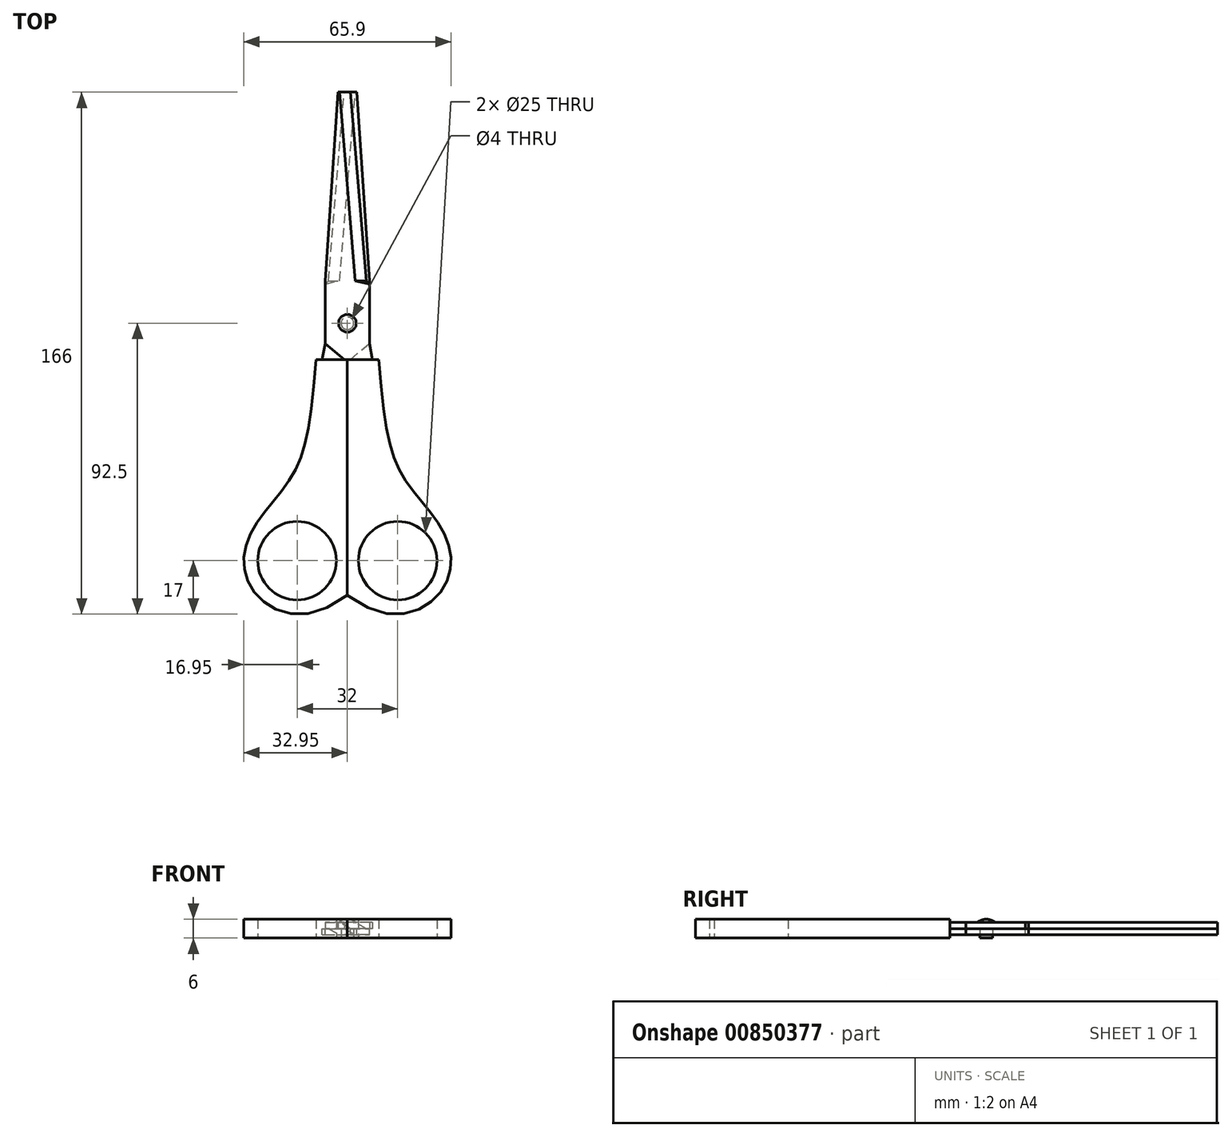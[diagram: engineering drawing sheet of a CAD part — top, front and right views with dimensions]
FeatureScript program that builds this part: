
annotation { "Feature Type Name" : "Feature", "Feature Type Description" : "" }
export const myFeature = defineFeature(function(context is Context, id is Id, definition is map)
    precondition{}
    {
        {
            var Q0;
            Q0=qCreatedBy(makeId("Top.planeOp"),FACE);
            var sketch = newSketch(context, id + "F0", { "sketchPlane" : qUnion([Q0])});
            skLineSegment(sketch, "E0", {"start": v(10, 0) * mm, "end": v(0, 0) * mm});
            skLineSegment(sketch, "E1", {"start": v(0, 0) * mm, "end": v(0, -75) * mm});
            skFitSpline(sketch, "E2", {"points": [v(10, 0) * mm, v(18.6, -38.65) * mm, v(31.21, -56.2) * mm, v(29.97, -73.56) * mm, v(0, -75) * mm], "startDerivative": vector(15.7, -213.23) * mm, "endDerivative": vector(-155.18, 117.57) * mm});
            skSolve(sketch);
        }
        {
            var Q0;
            Q0=qSketchRegion(id+"F0",true);
            extrude(context, id + "F1", {"entities" : qUnion([Q0]), "depth" : 6 * mm, "offsetDistance" : 25 * mm});
        }
        {
            var Q0;
            Q0=qCreatedBy(makeId("Top.planeOp"),FACE);
            var sketch = newSketch(context, id + "F2", { "sketchPlane" : qUnion([Q0])});
            skCircle(sketch, "E3", {"center": v(16, -64) * mm, "radius": 12.5 * mm});
            skSolve(sketch);
        }
        {
            var Q0;
            Q0=qSketchRegion(id+"F2",true);
            extrude(context, id + "F3", {"entities" : qUnion([Q0]), "depth" : 6 * mm, "offsetDistance" : 25 * mm});
        }
        {
            var Q0;
            Q0=makeQuery(id+"F3.opExtrude","SWEPT_BODY",BODY,{"disambiguationData":[OSD([sQuery(id+"F2.wireOp",EDGE,"E3")])]});
            var Q1;
            Q1=makeQuery(id+"F1.opExtrude","SWEPT_BODY",BODY,{"disambiguationData":[OSD([sQuery(id+"F0.wireOp",EDGE,"E0"),sQuery(id+"F0.wireOp",EDGE,"E1"),sQuery(id+"F0.wireOp",EDGE,"E2")])]});
            booleanBodies(context, id + "F4", {"operationType" : BooleanOperationType.SUBTRACTION, "tools" : qUnion([Q0]), "targets" : qUnion([Q1])});
        }
        {
            var Q0;
            Q0=makeQuery(id+"F1.opExtrude","SWEPT_BODY",BODY,{"disambiguationData":[OSD([sQuery(id+"F0.wireOp",EDGE,"E0"),sQuery(id+"F0.wireOp",EDGE,"E1"),sQuery(id+"F0.wireOp",EDGE,"E2")])]});
            var Q1;
            Q1=qCreatedBy(makeId("Right.planeOp"),FACE);
            mirror(context, id + "F5", {"entities" : qUnion([Q0]), "mirrorPlane" : qUnion([Q1])});
        }
        {
            var Q0;
            Q0=qCreatedBy(makeId("Top.planeOp"),FACE);
            cPlane(context, id + "F6", {"entities" : qUnion([Q0]), "cplaneType" : CPlaneType.OFFSET, "offset" : 3 * mm, "width" : 150 * mm, "height" : 150 * mm});
        }
        {
            var Q0;
            Q0=qCreatedBy(makeId("Front.planeOp"),FACE);
            cPlane(context, id + "F7", {"entities" : qUnion([Q0]), "cplaneType" : CPlaneType.OFFSET, "offset" : 5 * mm, "oppositeDirection" : true, "width" : 150 * mm, "height" : 150 * mm});
        }
        {
            var Q0;
            Q0=qCreatedBy(makeId("Front.planeOp"),FACE);
            cPlane(context, id + "F8", {"entities" : qUnion([Q0]), "cplaneType" : CPlaneType.OFFSET, "offset" : 15 * mm, "oppositeDirection" : true, "width" : 150 * mm, "height" : 150 * mm});
        }
        {
            var Q0;
            Q0=qCreatedBy(makeId("Front.planeOp"),FACE);
            cPlane(context, id + "F9", {"entities" : qUnion([Q0]), "cplaneType" : CPlaneType.OFFSET, "offset" : 25 * mm, "oppositeDirection" : true, "width" : 150 * mm, "height" : 150 * mm});
        }
        {
            var Q0;
            Q0=qCreatedBy(makeId("Front.planeOp"),FACE);
            cPlane(context, id + "F10", {"entities" : qUnion([Q0]), "cplaneType" : CPlaneType.OFFSET, "offset" : 85 * mm, "oppositeDirection" : true, "width" : 150 * mm, "height" : 150 * mm});
        }
        {
            var Q0;
            Q0=qCreatedBy(makeId("Front.planeOp"),FACE);
            cPlane(context, id + "F11", {"entities" : qUnion([Q0]), "cplaneType" : CPlaneType.OFFSET, "offset" : 24 * mm, "oppositeDirection" : true, "width" : 150 * mm, "height" : 150 * mm});
        }
        {
            var Q0;
            Q0=qCreatedBy(makeId("Front.planeOp"),FACE);
            var sketch = newSketch(context, id + "F12", { "sketchPlane" : qUnion([Q0])});
            skLineSegment(sketch, "E4.bottom", {"start": v(8, 5) * mm, "end": v(-1, 5) * mm});
            skLineSegment(sketch, "E4.top", {"start": v(8, 3) * mm, "end": v(-1, 3) * mm});
            skLineSegment(sketch, "E4.left", {"start": v(8, 5) * mm, "end": v(8, 3) * mm});
            skLineSegment(sketch, "E4.right", {"start": v(-1, 5) * mm, "end": v(-1, 3) * mm});
            skSolve(sketch);
        }
        {
            var Q0;
            Q0=qCreatedBy(id+"F7.planeOp",FACE);
            var sketch = newSketch(context, id + "F13", { "sketchPlane" : qUnion([Q0])});
            skLineSegment(sketch, "E5.bottom", {"start": v(7, 5) * mm, "end": v(-7, 5) * mm});
            skLineSegment(sketch, "E5.top", {"start": v(7, 3) * mm, "end": v(-7, 3) * mm});
            skLineSegment(sketch, "E5.left", {"start": v(7, 5) * mm, "end": v(7, 3) * mm});
            skLineSegment(sketch, "E5.right", {"start": v(-7, 5) * mm, "end": v(-7, 3) * mm});
            skSolve(sketch);
        }
        {
            var Q0;
            Q0=qCreatedBy(id+"F10.planeOp",FACE);
            var sketch = newSketch(context, id + "F14", { "sketchPlane" : qUnion([Q0])});
            skLineSegment(sketch, "E6", {"start": v(-2.5, 5) * mm, "end": v(-3, 5) * mm});
            skLineSegment(sketch, "E7", {"start": v(-3, 5) * mm, "end": v(-3, 3) * mm});
            skLineSegment(sketch, "E8", {"start": v(-3, 3) * mm, "end": v(1, 3) * mm});
            skLineSegment(sketch, "E9", {"start": v(1, 3) * mm, "end": v(-2.5, 5) * mm});
            skSolve(sketch);
        }
        {
            var Q0;
            Q0=qCreatedBy(id+"F8.planeOp",FACE);
            var sketch = newSketch(context, id + "F15", { "sketchPlane" : qUnion([Q0])});
            skLineSegment(sketch, "E10", {"start": v(-7, 5) * mm, "end": v(6, 5) * mm});
            skLineSegment(sketch, "E11", {"start": v(6, 5) * mm, "end": v(6, 3) * mm});
            skLineSegment(sketch, "E12", {"start": v(6, 3) * mm, "end": v(-7, 3) * mm});
            skLineSegment(sketch, "E13", {"start": v(-7, 3) * mm, "end": v(-7, 5) * mm});
            skSolve(sketch);
        }
        {
            var Q0;
            Q0=qCreatedBy(id+"F9.planeOp",FACE);
            var sketch = newSketch(context, id + "F16", { "sketchPlane" : qUnion([Q0])});
            skLineSegment(sketch, "E14", {"start": v(-7, 3) * mm, "end": v(6, 3) * mm});
            skLineSegment(sketch, "E15", {"start": v(6, 3) * mm, "end": v(2.5, 5) * mm});
            skLineSegment(sketch, "E16", {"start": v(2.5, 5) * mm, "end": v(-7, 5) * mm});
            skLineSegment(sketch, "E17", {"start": v(-7, 5) * mm, "end": v(-7, 3) * mm});
            skSolve(sketch);
        }
        {
            var Q0;
            Q0=qCreatedBy(id+"F11.planeOp",FACE);
            var sketch = newSketch(context, id + "F17", { "sketchPlane" : qUnion([Q0])});
            skLineSegment(sketch, "E18", {"start": v(-7, 5) * mm, "end": v(7, 5) * mm});
            skLineSegment(sketch, "E19", {"start": v(7, 5) * mm, "end": v(7, 3) * mm});
            skLineSegment(sketch, "E20", {"start": v(7, 3) * mm, "end": v(-7, 3) * mm});
            skLineSegment(sketch, "E21", {"start": v(-7, 3) * mm, "end": v(-7, 5) * mm});
            skSolve(sketch);
        }
        {
            var Q1;
            Q1=makeQuery(id+"F12.imprint","IMPRINT",FACE,{"disambiguationData":[TD([[makeQuery(id+"F12.imprint","IMPRINT",EDGE,{"derivedFrom":sQuery(id+"F12.wireOp",EDGE,"E4.bottom")}),1.0]])]});
            var Q2;
            Q2=makeQuery(id+"F13.imprint","IMPRINT",FACE,{"disambiguationData":[TD([[makeQuery(id+"F13.imprint","IMPRINT",EDGE,{"derivedFrom":sQuery(id+"F13.wireOp",EDGE,"E5.bottom")}),1.0]])]});
            loft(context, id + "F18", {"sheetProfilesArray" : [{ "sheetProfileEntities" : qUnion([Q1]) }, { "sheetProfileEntities" : qUnion([Q2]) }]});
        }
        {
            var Q0;
            Q0=qCreatedBy(id+"F6.planeOp",FACE);
            var sketch = newSketch(context, id + "F19", { "sketchPlane" : qUnion([Q0])});
            skLineSegment(sketch, "E22", {"start": v(0, 0) * mm, "end": v(0, 90) * mm});
            skSolve(sketch);
        }
        {
            var Q1;
            Q1=makeQuery(id+"F13.imprint","IMPRINT",FACE,{"disambiguationData":[TD([[makeQuery(id+"F13.imprint","IMPRINT",EDGE,{"derivedFrom":sQuery(id+"F13.wireOp",EDGE,"E5.bottom")}),1.0]])]});
            var Q2;
            Q2=makeQuery(id+"F17.imprint","IMPRINT",FACE,{"disambiguationData":[TD([[makeQuery(id+"F17.imprint","IMPRINT",EDGE,{"derivedFrom":sQuery(id+"F17.wireOp",EDGE,"E18")}),-1.0]])]});
            loft(context, id + "F20", {"operationType" : NewBodyOperationType.ADD, "sheetProfilesArray" : [{ "sheetProfileEntities" : qUnion([Q1]) }, { "sheetProfileEntities" : qUnion([Q2]) }]});
        }
        {
            var Q1;
            Q1=makeQuery(id+"F20.opLoft","CAP_FACE",FACE,{"disambiguationData":[OSD([makeQuery(id+"F17.imprint","IMPRINT",FACE,{"disambiguationData":[TD([[makeQuery(id+"F17.imprint","IMPRINT",EDGE,{"derivedFrom":sQuery(id+"F17.wireOp",EDGE,"E18")}),-1.0]])]})])],"isStart":true});
            var Q2;
            Q2=makeQuery(id+"F16.imprint","IMPRINT",FACE,{"disambiguationData":[TD([[makeQuery(id+"F16.imprint","IMPRINT",EDGE,{"derivedFrom":sQuery(id+"F16.wireOp",EDGE,"E14")}),1.0]])]});
            loft(context, id + "F21", {"operationType" : NewBodyOperationType.ADD, "sheetProfilesArray" : [{ "sheetProfileEntities" : qUnion([Q1]) }, { "sheetProfileEntities" : qUnion([Q2]) }]});
        }
        {
            var Q1;
            Q1=makeQuery(id+"F21.opLoft","CAP_FACE",FACE,{"disambiguationData":[OSD([makeQuery(id+"F16.imprint","IMPRINT",FACE,{"disambiguationData":[TD([[makeQuery(id+"F16.imprint","IMPRINT",EDGE,{"derivedFrom":sQuery(id+"F16.wireOp",EDGE,"E14")}),1.0]])]})])],"isStart":true});
            var Q2;
            Q2=makeQuery(id+"F14.imprint","IMPRINT",FACE,{"disambiguationData":[TD([[makeQuery(id+"F14.imprint","IMPRINT",EDGE,{"derivedFrom":sQuery(id+"F14.wireOp",EDGE,"E6")}),1.0]])]});
            loft(context, id + "F22", {"operationType" : NewBodyOperationType.ADD, "sheetProfilesArray" : [{ "sheetProfileEntities" : qUnion([Q1]) }, { "sheetProfileEntities" : qUnion([Q2]) }]});
        }
        {
            var Q0;
            Q0=makeQuery(id+"F18.opLoft","SWEPT_BODY",BODY,{"disambiguationData":[OSD([makeQuery(id+"F12.imprint","IMPRINT",FACE,{"disambiguationData":[TD([[makeQuery(id+"F12.imprint","IMPRINT",EDGE,{"derivedFrom":sQuery(id+"F12.wireOp",EDGE,"E4.bottom")}),1.0]])]}),makeQuery(id+"F13.imprint","IMPRINT",FACE,{"disambiguationData":[TD([[makeQuery(id+"F13.imprint","IMPRINT",EDGE,{"derivedFrom":sQuery(id+"F13.wireOp",EDGE,"E5.bottom")}),1.0]])]})])]});
            var Q1;
            Q1=sQuery(id+"F19.wireOp",EDGE,"E22");
            transform(context, id + "F23", {"entities" : qUnion([Q0]), "transformType" : TransformType.ROTATION, "transformAxis" : qUnion([Q1]), "angle" : 180 * degree, "makeCopy" : true});
        }
        {
            var Q0;
            Q0=qCreatedBy(makeId("Top.planeOp"),FACE);
            var sketch = newSketch(context, id + "F24", { "sketchPlane" : qUnion([Q0])});
            skCircle(sketch, "E23", {"center": v(0, 11.5) * mm, "radius": 2 * mm});
            skSolve(sketch);
        }
        {
            var Q0;
            Q0=qSketchRegion(id+"F24",true);
            extrude(context, id + "F25", {"entities" : qUnion([Q0]), "depth" : 5.5 * mm, "offsetDistance" : 25 * mm});
        }
        {
            var Q0;
            Q0=makeQuery(id+"F25.opExtrude","SWEPT_BODY",BODY,{"disambiguationData":[OSD([sQuery(id+"F24.wireOp",EDGE,"E23")])]});
            var Q1;
            Q1=makeQuery(id+"F18.opLoft","SWEPT_BODY",BODY,{"disambiguationData":[OSD([makeQuery(id+"F12.imprint","IMPRINT",FACE,{"disambiguationData":[TD([[makeQuery(id+"F12.imprint","IMPRINT",EDGE,{"derivedFrom":sQuery(id+"F12.wireOp",EDGE,"E4.bottom")}),1.0]])]}),makeQuery(id+"F13.imprint","IMPRINT",FACE,{"disambiguationData":[TD([[makeQuery(id+"F13.imprint","IMPRINT",EDGE,{"derivedFrom":sQuery(id+"F13.wireOp",EDGE,"E5.bottom")}),1.0]])]})])]});
            var Q2;
            Q2=makeQuery(id+"F23.opPattern","COPY",BODY,{"derivedFrom":makeQuery(id+"F18.opLoft","SWEPT_BODY",BODY,{"disambiguationData":[OSD([makeQuery(id+"F12.imprint","IMPRINT",FACE,{"disambiguationData":[TD([[makeQuery(id+"F12.imprint","IMPRINT",EDGE,{"derivedFrom":sQuery(id+"F12.wireOp",EDGE,"E4.bottom")}),1.0]])]}),makeQuery(id+"F13.imprint","IMPRINT",FACE,{"disambiguationData":[TD([[makeQuery(id+"F13.imprint","IMPRINT",EDGE,{"derivedFrom":sQuery(id+"F13.wireOp",EDGE,"E5.bottom")}),1.0]])]})])]}),"instanceName":"1"});
            booleanBodies(context, id + "F26", {"operationType" : BooleanOperationType.SUBTRACTION, "tools" : qUnion([Q0]), "targets" : qUnion([Q1, Q2]), "keepTools" : true});
        }
        {
            var Q0;
            Q0=qCreatedBy(makeId("Front.planeOp"),FACE);
            cPlane(context, id + "F27", {"entities" : qUnion([Q0]), "cplaneType" : CPlaneType.OFFSET, "offset" : 11.5 * mm, "oppositeDirection" : true, "width" : 150 * mm, "height" : 150 * mm});
        }
        {
            var Q0;
            Q0=qCreatedBy(id+"F27.planeOp",FACE);
            var sketch = newSketch(context, id + "F28", { "sketchPlane" : qUnion([Q0])});
            skArc(sketch, "E24", {"start": v(2.8, 5) * mm, "mid": v(1.49, 5.74) * mm, "end": v(0, 6) * mm});
            skLineSegment(sketch, "E25", {"start": v(2.8, 5) * mm, "end": v(0, 5) * mm});
            skLineSegment(sketch, "E26", {"start": v(0, 5) * mm, "end": v(0, 6) * mm});
            skSolve(sketch);
        }
        {
            var Q0;
            Q0=makeQuery(id+"F28.imprint","IMPRINT",FACE,{"disambiguationData":[TD([[makeQuery(id+"F28.imprint","IMPRINT",EDGE,{"derivedFrom":sQuery(id+"F28.wireOp",EDGE,"E24")}),1.0]])]});
            var Q1;
            Q1=sQuery(id+"F28.wireOp",EDGE,"E26");
            revolve(context, id + "F29", {"operationType" : NewBodyOperationType.ADD, "surfaceOperationType" : NewSurfaceOperationType.NEW, "entities" : qUnion([Q0]), "axis" : qUnion([Q1]), "revolveType" : RevolveType.FULL});
        }
    });
